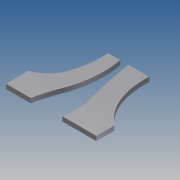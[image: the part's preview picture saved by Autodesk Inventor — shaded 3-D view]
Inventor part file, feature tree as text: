
AUTODESK INVENTOR PART (.ipt)
format: ipt  version: 2014 (Build 180170000, 170)  size: 138,240 bytes
history: native  units: mm
features: extrude x1
ambient origin geometry x8: Origin, YZ Plane, XZ Plane, XY Plane, X Axis, Y Axis, Z Axis, Center Point
bodies: Body1 (feature_tree)
feature tree (1):
  extrude  "Extrusion9"  Depth=1000.0mm
